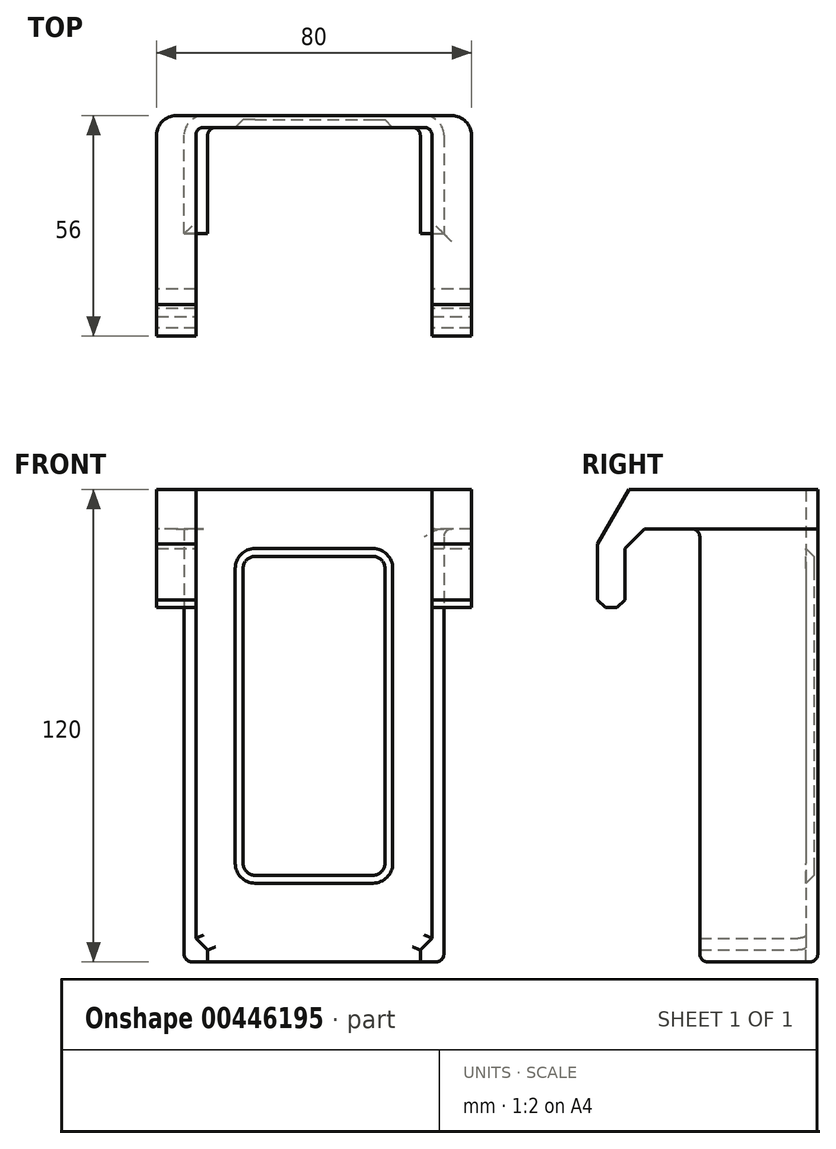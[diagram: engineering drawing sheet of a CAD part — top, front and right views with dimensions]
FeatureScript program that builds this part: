
annotation { "Feature Type Name" : "Feature", "Feature Type Description" : "" }
export const myFeature = defineFeature(function(context is Context, id is Id, definition is map)
    precondition{}
    {
        {
            var Q0;
            Q0=qCreatedBy(makeId("Top.planeOp"),FACE);
            var sketch = newSketch(context, id + "F0", { "sketchPlane" : qUnion([Q0])});
            skLineSegment(sketch, "E0", {"start": v(-33, 0) * mm, "end": v(-33, 30) * mm});
            skLineSegment(sketch, "E1", {"start": v(-33, 30) * mm, "end": v(33, 30) * mm});
            skLineSegment(sketch, "E2", {"start": v(33, 30) * mm, "end": v(33, 0) * mm});
            skLineSegment(sketch, "E3", {"start": v(0, 0) * mm, "end": v(0, 30) * mm, "construction": true});
            skLineSegment(sketch, "E4", {"start": v(-33, 0) * mm, "end": v(33, 0) * mm});
            skSolve(sketch);
        }
        {
            var Q0;
            Q0 = qSketchRegion(id + "F0", true);
            extrude(context, id + "F1", {"entities" : qUnion([Q0]), "depth" : 120 * mm});
        }
        {
            var Q0;
            Q0=makeQuery(id+"F1.opExtrude","SWEPT_FACE",FACE,{"disambiguationData":[OSD([sQuery(id+"F0.wireOp",EDGE,"E4")])]});
            var Q1;
            Q1=makeQuery(id+"F1.opExtrude","CAP_FACE",FACE,{"disambiguationData":[OSD([sQuery(id+"F0.wireOp",EDGE,"E0"),sQuery(id+"F0.wireOp",EDGE,"E1"),sQuery(id+"F0.wireOp",EDGE,"E2"),sQuery(id+"F0.wireOp",EDGE,"E4")])],"isStart":false});
            shell(context, id + "F2", {"entities" : qUnion([Q0, Q1]), "thickness" : 3 * mm});
        }
        {
            var Q0;
            Q0=makeQuery(id+"F2.opShell","OFFSET_FACE",FACE,{"disambiguationData":[OSD([sQuery(id+"F0.wireOp",EDGE,"E0"),sQuery(id+"F0.wireOp",EDGE,"E1"),sQuery(id+"F0.wireOp",EDGE,"E2"),sQuery(id+"F0.wireOp",EDGE,"E4")])]});
            var sketch = newSketch(context, id + "F3", { "sketchPlane" : qUnion([Q0])});
            skLineSegment(sketch, "E5.bottom", {"start": v(-27, 0) * mm, "end": v(27, 0) * mm});
            skLineSegment(sketch, "E5.top", {"start": v(-27, 27) * mm, "end": v(27, 27) * mm});
            skLineSegment(sketch, "E5.left", {"start": v(-27, 0) * mm, "end": v(-27, 27) * mm});
            skLineSegment(sketch, "E5.right", {"start": v(27, 0) * mm, "end": v(27, 27) * mm});
            skSolve(sketch);
        }
        {
            var Q0;
            Q0 = qSketchRegion(id + "F3", true);
            extrude(context, id + "F4", {"entities" : qUnion([Q0]), "operationType" : NewBodyOperationType.REMOVE, "endBound" : BoundingType.THROUGH_ALL, "oppositeDirection" : true, "depth" : 25 * mm});
        }
        {
            var Q0;
            Q0=makeQuery(id+"F4.boolean.opBoolean","MERGE",FACE,{"derivedFrom":[makeQuery(id+"F2.opShell","OFFSET_FACE",FACE,{"disambiguationData":[OSD([sQuery(id+"F0.wireOp",EDGE,"E1")])]}),makeQuery(id+"F4.opExtrude","SWEPT_FACE",FACE,{"disambiguationData":[OSD([sQuery(id+"F3.wireOp",EDGE,"E5.top")])]})]});
            var sketch = newSketch(context, id + "F5", { "sketchPlane" : qUnion([Q0])});
            skLineSegment(sketch, "E6.top", {"start": v(-20, 20) * mm, "end": v(20, 20) * mm});
            skLineSegment(sketch, "E6.left", {"start": v(-20, 105) * mm, "end": v(-20, 20) * mm});
            skLineSegment(sketch, "E6.right", {"start": v(20, 105) * mm, "end": v(20, 20) * mm});
            skLineSegment(sketch, "E7", {"start": v(0, 20) * mm, "end": v(0, 0) * mm, "construction": true});
            skLineSegment(sketch, "E8", {"start": v(-20, 105) * mm, "end": v(20, 105) * mm});
            skSolve(sketch);
        }
        {
            var Q0;
            Q0 = qSketchRegion(id + "F5", true);
            extrude(context, id + "F6", {"entities" : qUnion([Q0]), "operationType" : NewBodyOperationType.REMOVE, "oppositeDirection" : true, "depth" : 2 * mm});
        }
        {
            var Q0;
            Q0=makeQuery(id+"F2.opShell","OFFSET_FACE",FACE,{"disambiguationData":[OSD([sQuery(id+"F0.wireOp",EDGE,"E2")])]});
            var sketch = newSketch(context, id + "F7", { "sketchPlane" : qUnion([Q0])});
            skLineSegment(sketch, "E9", {"start": v(-30, 120) * mm, "end": v(26, 120) * mm});
            skLineSegment(sketch, "E10", {"start": v(26, 120) * mm, "end": v(26, 90) * mm});
            skLineSegment(sketch, "E11", {"start": v(26, 90) * mm, "end": v(19, 90) * mm});
            skLineSegment(sketch, "E12", {"start": v(19, 90) * mm, "end": v(19, 110) * mm});
            skLineSegment(sketch, "E13", {"start": v(19, 110) * mm, "end": v(-30, 110) * mm});
            skLineSegment(sketch, "E14", {"start": v(-30, 110) * mm, "end": v(-30, 120) * mm});
            skSolve(sketch);
        }
        {
            var Q0;
            Q0 = qSketchRegion(id + "F7", true);
            extrude(context, id + "F8", {"entities" : qUnion([Q0]), "operationType" : NewBodyOperationType.ADD, "oppositeDirection" : true, "depth" : 10 * mm});
        }
        {
            var Q0;
            Q0=makeQuery(id+"F1.opExtrude","SWEPT_BODY",BODY,{"disambiguationData":[OSD([sQuery(id+"F0.wireOp",EDGE,"E0"),sQuery(id+"F0.wireOp",EDGE,"E1"),sQuery(id+"F0.wireOp",EDGE,"E2"),sQuery(id+"F0.wireOp",EDGE,"E4")])]});
            var Q1;
            Q1=qCreatedBy(makeId("Right.planeOp"),FACE);
            mirror(context, id + "F9", {"operationType" : NewBodyOperationType.ADD, "entities" : qUnion([Q0]), "mirrorPlane" : qUnion([Q1])});
        }
        {
            var Q0;
            Q0=makeQuery(id+"F1.opExtrude","SWEPT_EDGE",EDGE,{"disambiguationData":[OSD([sQuery(id+"F0.wireOp",EDGE,"E1"),sQuery(id+"F0.wireOp",EDGE,"E2")])]});
            var Q1;
            Q1=makeQuery(id+"F1.opExtrude","SWEPT_EDGE",EDGE,{"disambiguationData":[OSD([sQuery(id+"F0.wireOp",EDGE,"E0"),sQuery(id+"F0.wireOp",EDGE,"E1")])]});
            fillet(context, id + "F10", {"entities" : qUnion([Q0, Q1]), "radius" : 5 * mm, "tangentPropagation" : true, "allowEdgeOverflow" : false});
        }
        {
            var Q0;
            {var subQ0=sQuery(id+"F0.wireOp",EDGE,"E0");Q0=makeQuery(id+"F2.opShell","OFFSET_EDGE",EDGE,{"disambiguationData":[OSD([subQ0]),TDD([makeQuery(id+"F1.opExtrude","CAP_EDGE",EDGE,{"disambiguationData":[OSD([subQ0])],"isStart":true})])]});}
            var Q1;
            {var subQ0=sQuery(id+"F0.wireOp",EDGE,"E2");Q1=makeQuery(id+"F2.opShell","OFFSET_EDGE",EDGE,{"disambiguationData":[OSD([subQ0]),TDD([makeQuery(id+"F1.opExtrude","CAP_EDGE",EDGE,{"disambiguationData":[OSD([subQ0])],"isStart":true})])]});}
            chamfer(context, id + "F11", {"entities" : qUnion([Q0, Q1]), "width" : 3 * mm, "tangentPropagation" : true});
        }
        {
            var Q0;
            Q0=makeQuery(id+"F9.opPattern","COPY",EDGE,{"derivedFrom":makeQuery(id+"F8.opExtrude","SWEPT_EDGE",EDGE,{"disambiguationData":[OSD([sQuery(id+"F7.wireOp",EDGE,"E9"),sQuery(id+"F7.wireOp",EDGE,"E10")])]}),"instanceName":"1"});
            var Q1;
            Q1=makeQuery(id+"F8.opExtrude","SWEPT_EDGE",EDGE,{"disambiguationData":[OSD([sQuery(id+"F7.wireOp",EDGE,"E9"),sQuery(id+"F7.wireOp",EDGE,"E10")])]});
            chamfer(context, id + "F12", {"entities" : qUnion([Q0, Q1]), "chamferType" : ChamferType.OFFSET_ANGLE, "width" : 8 * mm, "oppositeDirection" : false, "angle" : 60 * degree, "tangentPropagation" : true});
        }
        {
            var Q0;
            Q0=makeQuery(id+"F8.opExtrude","SWEPT_EDGE",EDGE,{"disambiguationData":[OSD([sQuery(id+"F7.wireOp",EDGE,"E12"),sQuery(id+"F7.wireOp",EDGE,"E13")])]});
            var Q1;
            Q1=makeQuery(id+"F9.opPattern","COPY",EDGE,{"derivedFrom":makeQuery(id+"F8.opExtrude","SWEPT_EDGE",EDGE,{"disambiguationData":[OSD([sQuery(id+"F7.wireOp",EDGE,"E12"),sQuery(id+"F7.wireOp",EDGE,"E13")])]}),"instanceName":"1"});
            chamfer(context, id + "F13", {"entities" : qUnion([Q0, Q1]), "width" : 5 * mm, "tangentPropagation" : true});
        }
        {
            var Q0;
            Q0=makeQuery(id+"F9.opPattern","COPY",EDGE,{"derivedFrom":makeQuery(id+"F8.opExtrude","SWEPT_EDGE",EDGE,{"disambiguationData":[OSD([sQuery(id+"F7.wireOp",EDGE,"E11"),sQuery(id+"F7.wireOp",EDGE,"E12")])]}),"instanceName":"1"});
            var Q1;
            Q1=makeQuery(id+"F9.opPattern","COPY",EDGE,{"derivedFrom":makeQuery(id+"F8.opExtrude","SWEPT_EDGE",EDGE,{"disambiguationData":[OSD([sQuery(id+"F7.wireOp",EDGE,"E10"),sQuery(id+"F7.wireOp",EDGE,"E11")])]}),"instanceName":"1"});
            var Q2;
            Q2=makeQuery(id+"F8.opExtrude","SWEPT_EDGE",EDGE,{"disambiguationData":[OSD([sQuery(id+"F7.wireOp",EDGE,"E11"),sQuery(id+"F7.wireOp",EDGE,"E12")])]});
            var Q3;
            Q3=makeQuery(id+"F8.opExtrude","SWEPT_EDGE",EDGE,{"disambiguationData":[OSD([sQuery(id+"F7.wireOp",EDGE,"E10"),sQuery(id+"F7.wireOp",EDGE,"E11")])]});
            chamfer(context, id + "F14", {"entities" : qUnion([Q0, Q1, Q2, Q3]), "width" : 2 * mm, "tangentPropagation" : true});
        }
        {
            var Q0;
            Q0=makeQuery(id+"F8.opExtrude","CAP_EDGE",EDGE,{"disambiguationData":[OSD([sQuery(id+"F7.wireOp",EDGE,"E14")])],"isStart":false});
            var Q1;
            Q1=makeQuery(id+"F9.opPattern","COPY",EDGE,{"derivedFrom":makeQuery(id+"F8.opExtrude","CAP_EDGE",EDGE,{"disambiguationData":[OSD([sQuery(id+"F7.wireOp",EDGE,"E14")])],"isStart":false}),"instanceName":"1"});
            fillet(context, id + "F15", {"entities" : qUnion([Q0, Q1]), "radius" : 5 * mm, "tangentPropagation" : true, "allowEdgeOverflow" : false});
        }
        {
            var Q0;
            Q0=makeQuery(id+"F2.opShell","OFFSET_EDGE",EDGE,{"disambiguationData":[OSD([sQuery(id+"F0.wireOp",EDGE,"E1"),sQuery(id+"F0.wireOp",EDGE,"E2")])]});
            var Q1;
            Q1=makeQuery(id+"F2.opShell","OFFSET_EDGE",EDGE,{"disambiguationData":[OSD([sQuery(id+"F0.wireOp",EDGE,"E0"),sQuery(id+"F0.wireOp",EDGE,"E1")])]});
            var Q2;
            {var subQ0=sQuery(id+"F0.wireOp",EDGE,"E0");Q2=makeQuery(id+"F11.opChamfer","BLEND_EDGE",EDGE,{"blendedFrom":[makeQuery(id+"F2.opShell","OFFSET_EDGE",EDGE,{"disambiguationData":[OSD([subQ0]),TDD([makeQuery(id+"F1.opExtrude","CAP_EDGE",EDGE,{"disambiguationData":[OSD([subQ0])],"isStart":true})])]}),makeQuery(id+"F4.boolean.opBoolean","MERGE",FACE,{"derivedFrom":[makeQuery(id+"F2.opShell","OFFSET_FACE",FACE,{"disambiguationData":[OSD([sQuery(id+"F0.wireOp",EDGE,"E1")])]}),makeQuery(id+"F4.opExtrude","SWEPT_FACE",FACE,{"disambiguationData":[OSD([sQuery(id+"F3.wireOp",EDGE,"E5.top")])]})]})],"blendedInto":[makeQuery(id+"F4.boolean.opBoolean","MERGE",FACE,{"derivedFrom":[makeQuery(id+"F2.opShell","OFFSET_FACE",FACE,{"disambiguationData":[OSD([sQuery(id+"F0.wireOp",EDGE,"E1")])]}),makeQuery(id+"F4.opExtrude","SWEPT_FACE",FACE,{"disambiguationData":[OSD([sQuery(id+"F3.wireOp",EDGE,"E5.top")])]})]})]});}
            var Q3;
            {var subQ0=sQuery(id+"F0.wireOp",EDGE,"E2");Q3=makeQuery(id+"F11.opChamfer","BLEND_EDGE",EDGE,{"blendedFrom":[makeQuery(id+"F2.opShell","OFFSET_EDGE",EDGE,{"disambiguationData":[OSD([subQ0]),TDD([makeQuery(id+"F1.opExtrude","CAP_EDGE",EDGE,{"disambiguationData":[OSD([subQ0])],"isStart":true})])]}),makeQuery(id+"F4.boolean.opBoolean","MERGE",FACE,{"derivedFrom":[makeQuery(id+"F2.opShell","OFFSET_FACE",FACE,{"disambiguationData":[OSD([sQuery(id+"F0.wireOp",EDGE,"E1")])]}),makeQuery(id+"F4.opExtrude","SWEPT_FACE",FACE,{"disambiguationData":[OSD([sQuery(id+"F3.wireOp",EDGE,"E5.top")])]})]})],"blendedInto":[makeQuery(id+"F4.boolean.opBoolean","MERGE",FACE,{"derivedFrom":[makeQuery(id+"F2.opShell","OFFSET_FACE",FACE,{"disambiguationData":[OSD([sQuery(id+"F0.wireOp",EDGE,"E1")])]}),makeQuery(id+"F4.opExtrude","SWEPT_FACE",FACE,{"disambiguationData":[OSD([sQuery(id+"F3.wireOp",EDGE,"E5.top")])]})]})]});}
            var Q4;
            Q4=makeQuery(id+"F4.boolean.opBoolean","COPY",EDGE,{"derivedFrom":makeQuery(id+"F4.opExtrude","SWEPT_EDGE",EDGE,{"disambiguationData":[OSD([sQuery(id+"F0.wireOp",EDGE,"E1"),sQuery(id+"F3.wireOp",EDGE,"E5.top"),sQuery(id+"F3.wireOp",EDGE,"E5.left")])]})});
            var Q5;
            Q5=makeQuery(id+"F4.boolean.opBoolean","COPY",EDGE,{"derivedFrom":makeQuery(id+"F4.opExtrude","SWEPT_EDGE",EDGE,{"disambiguationData":[OSD([sQuery(id+"F0.wireOp",EDGE,"E1"),sQuery(id+"F3.wireOp",EDGE,"E5.top"),sQuery(id+"F3.wireOp",EDGE,"E5.right")])]})});
            fillet(context, id + "F16", {"entities" : qUnion([Q0, Q1, Q2, Q3, Q4, Q5]), "radius" : 2 * mm, "tangentPropagation" : true, "allowEdgeOverflow" : false});
        }
        {
            var Q0;
            {var subQ0=sQuery(id+"F0.wireOp",EDGE,"E0");Q0=makeQuery(id+"F16.opFillet","BLEND_EDGE",EDGE,{"blendedFrom":[makeQuery(id+"F2.opShell","OFFSET_EDGE",EDGE,{"disambiguationData":[OSD([subQ0,sQuery(id+"F0.wireOp",EDGE,"E1")])]}),makeQuery(id+"F9.boolean.opBoolean","MERGE",FACE,{"derivedFrom":[makeQuery(id+"F2.opShell","OFFSET_FACE",FACE,{"disambiguationData":[OSD([subQ0])]}),makeQuery(id+"F9.opPattern","COPY",FACE,{"derivedFrom":makeQuery(id+"F8.boolean.opBoolean","MERGE",FACE,{"derivedFrom":[makeQuery(id+"F2.opShell","OFFSET_FACE",FACE,{"disambiguationData":[OSD([sQuery(id+"F0.wireOp",EDGE,"E2")])]}),makeQuery(id+"F8.opExtrude","CAP_FACE",FACE,{"disambiguationData":[OSD([sQuery(id+"F7.wireOp",EDGE,"E9"),sQuery(id+"F7.wireOp",EDGE,"E10"),sQuery(id+"F7.wireOp",EDGE,"E11"),sQuery(id+"F7.wireOp",EDGE,"E12"),sQuery(id+"F7.wireOp",EDGE,"E13"),sQuery(id+"F7.wireOp",EDGE,"E14")])],"isStart":true})]}),"instanceName":"1"})]})],"blendedInto":[makeQuery(id+"F9.boolean.opBoolean","MERGE",FACE,{"derivedFrom":[makeQuery(id+"F2.opShell","OFFSET_FACE",FACE,{"disambiguationData":[OSD([subQ0])]}),makeQuery(id+"F9.opPattern","COPY",FACE,{"derivedFrom":makeQuery(id+"F8.boolean.opBoolean","MERGE",FACE,{"derivedFrom":[makeQuery(id+"F2.opShell","OFFSET_FACE",FACE,{"disambiguationData":[OSD([sQuery(id+"F0.wireOp",EDGE,"E2")])]}),makeQuery(id+"F8.opExtrude","CAP_FACE",FACE,{"disambiguationData":[OSD([sQuery(id+"F7.wireOp",EDGE,"E9"),sQuery(id+"F7.wireOp",EDGE,"E10"),sQuery(id+"F7.wireOp",EDGE,"E11"),sQuery(id+"F7.wireOp",EDGE,"E12"),sQuery(id+"F7.wireOp",EDGE,"E13"),sQuery(id+"F7.wireOp",EDGE,"E14")])],"isStart":true})]}),"instanceName":"1"})]})]});}
            var Q1;
            Q1=makeQuery(id+"F8.boolean.opBoolean","INTERSECT",EDGE,{"derivedFrom":[makeQuery(id+"F1.opExtrude","SWEPT_FACE",FACE,{"disambiguationData":[OSD([sQuery(id+"F0.wireOp",EDGE,"E2")])]}),makeQuery(id+"F8.opExtrude","SWEPT_FACE",FACE,{"disambiguationData":[OSD([sQuery(id+"F7.wireOp",EDGE,"E13")])]})]});
            var Q2;
            Q2=makeQuery(id+"F9.opPattern","COPY",EDGE,{"derivedFrom":makeQuery(id+"F8.boolean.opBoolean","INTERSECT",EDGE,{"derivedFrom":[makeQuery(id+"F1.opExtrude","SWEPT_FACE",FACE,{"disambiguationData":[OSD([sQuery(id+"F0.wireOp",EDGE,"E2")])]}),makeQuery(id+"F8.opExtrude","SWEPT_FACE",FACE,{"disambiguationData":[OSD([sQuery(id+"F7.wireOp",EDGE,"E13")])]})]}),"instanceName":"1"});
            var Q3;
            {var subQ0=sQuery(id+"F0.wireOp",EDGE,"E2");var subQ1=sQuery(id+"F0.wireOp",EDGE,"E4");Q3=makeQuery(id+"F9.opPattern","COPY",EDGE,{"derivedFrom":makeQuery(id+"F8.boolean.opBoolean","INTERSECT",EDGE,{"derivedFrom":[makeQuery(id+"F4.boolean.opBoolean","SPLIT",FACE,{"disambiguationData":[TD([makeQuery(id+"F1.opExtrude","SWEPT_FACE",FACE,{"disambiguationData":[OSD([subQ0])]})])],"derivedFrom":makeQuery(id+"F1.opExtrude","SWEPT_FACE",FACE,{"disambiguationData":[OSD([subQ1])]})}),makeQuery(id+"F8.opExtrude","SWEPT_FACE",FACE,{"disambiguationData":[OSD([sQuery(id+"F7.wireOp",EDGE,"E13")])]})]}),"instanceName":"1"});}
            var Q4;
            {var subQ0=sQuery(id+"F0.wireOp",EDGE,"E2");var subQ1=sQuery(id+"F0.wireOp",EDGE,"E4");Q4=makeQuery(id+"F8.boolean.opBoolean","INTERSECT",EDGE,{"derivedFrom":[makeQuery(id+"F4.boolean.opBoolean","SPLIT",FACE,{"disambiguationData":[TD([makeQuery(id+"F1.opExtrude","SWEPT_FACE",FACE,{"disambiguationData":[OSD([subQ0])]})])],"derivedFrom":makeQuery(id+"F1.opExtrude","SWEPT_FACE",FACE,{"disambiguationData":[OSD([subQ1])]})}),makeQuery(id+"F8.opExtrude","SWEPT_FACE",FACE,{"disambiguationData":[OSD([sQuery(id+"F7.wireOp",EDGE,"E13")])]})]});}
            var Q5;
            {var subQ0=sQuery(id+"F0.wireOp",EDGE,"E0");var subQ1=sQuery(id+"F0.wireOp",EDGE,"E4");Q5=makeQuery(id+"F4.boolean.opBoolean","SPLIT",EDGE,{"disambiguationData":[TD([makeQuery(id+"F1.opExtrude","SWEPT_FACE",FACE,{"disambiguationData":[OSD([subQ0])]})])],"derivedFrom":makeQuery(id+"F1.opExtrude","CAP_EDGE",EDGE,{"disambiguationData":[OSD([subQ1])],"isStart":true})});}
            var Q6;
            {var subQ0=sQuery(id+"F0.wireOp",EDGE,"E4");var subQ1=sQuery(id+"F0.wireOp",EDGE,"E2");Q6=makeQuery(id+"F4.boolean.opBoolean","SPLIT",EDGE,{"disambiguationData":[TD([makeQuery(id+"F1.opExtrude","SWEPT_FACE",FACE,{"disambiguationData":[OSD([subQ1])]})])],"derivedFrom":makeQuery(id+"F1.opExtrude","CAP_EDGE",EDGE,{"disambiguationData":[OSD([subQ0])],"isStart":true})});}
            var Q7;
            Q7=makeQuery(id+"F1.opExtrude","CAP_EDGE",EDGE,{"disambiguationData":[OSD([sQuery(id+"F0.wireOp",EDGE,"E0")])],"isStart":true});
            fillet(context, id + "F17", {"entities" : qUnion([Q0, Q1, Q2, Q3, Q4, Q5, Q6, Q7]), "radius" : 2 * mm, "tangentPropagation" : true, "allowEdgeOverflow" : false});
        }
        {
            var Q0;
            Q0=makeQuery(id+"F6.boolean.opBoolean","COPY",EDGE,{"derivedFrom":makeQuery(id+"F6.opExtrude","SWEPT_EDGE",EDGE,{"disambiguationData":[OSD([sQuery(id+"F5.wireOp",EDGE,"E6.right"),sQuery(id+"F5.wireOp",EDGE,"E8")])]})});
            var Q1;
            Q1=makeQuery(id+"F6.boolean.opBoolean","COPY",EDGE,{"derivedFrom":makeQuery(id+"F6.opExtrude","SWEPT_EDGE",EDGE,{"disambiguationData":[OSD([sQuery(id+"F5.wireOp",EDGE,"E6.left"),sQuery(id+"F5.wireOp",EDGE,"E8")])]})});
            var Q2;
            Q2=makeQuery(id+"F6.boolean.opBoolean","COPY",EDGE,{"derivedFrom":makeQuery(id+"F6.opExtrude","SWEPT_EDGE",EDGE,{"disambiguationData":[OSD([sQuery(id+"F5.wireOp",EDGE,"E6.top"),sQuery(id+"F5.wireOp",EDGE,"E6.left")])]})});
            var Q3;
            Q3=makeQuery(id+"F6.boolean.opBoolean","COPY",EDGE,{"derivedFrom":makeQuery(id+"F6.opExtrude","SWEPT_EDGE",EDGE,{"disambiguationData":[OSD([sQuery(id+"F5.wireOp",EDGE,"E6.top"),sQuery(id+"F5.wireOp",EDGE,"E6.right")])]})});
            fillet(context, id + "F18", {"entities" : qUnion([Q0, Q1, Q2, Q3]), "radius" : 5 * mm, "tangentPropagation" : true, "allowEdgeOverflow" : false});
        }
        {
            var Q0;
            Q0=makeQuery(id+"F6.boolean.opBoolean","COPY",FACE,{"derivedFrom":makeQuery(id+"F6.opExtrude","CAP_FACE",FACE,{"disambiguationData":[OSD([sQuery(id+"F5.wireOp",EDGE,"E6.top"),sQuery(id+"F5.wireOp",EDGE,"E6.left"),sQuery(id+"F5.wireOp",EDGE,"E6.right"),sQuery(id+"F5.wireOp",EDGE,"E8")])],"isStart":false})});
            chamfer(context, id + "F19", {"entities" : qUnion([Q0]), "width" : 2 * mm, "tangentPropagation" : true});
        }
    });
